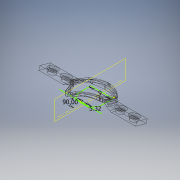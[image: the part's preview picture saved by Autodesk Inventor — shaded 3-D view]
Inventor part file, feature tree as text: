
AUTODESK INVENTOR PART (.ipt)
format: ipt  version: 2018 (Build 220112000, 112)  size: 2,753,024 bytes
history: native  units: mm
features: sketch x76, extrude x70, fillet x42, mirror x4, shell x1, hole x1, plane x1
ambient origin geometry x8: Origin, YZ Plane, XZ Plane, XY Plane, X Axis, Y Axis, Z Axis, Center Point
bodies: Solid1 (feature_tree)
feature tree (195):
  extrude  "Extrusion1"  TaperAngle=0.0deg  [1 undecoded]
  extrude  "Extrusion2"  Depth=10.0mm
  extrude  "Extrusion3"  TaperAngle=0.0deg  [1 undecoded]
  shell  "Shell2"  Thickness=0.0mm
  extrude  "Extrusion4"  Depth=1.6mm
  extrude  "Extrusion6"  Depth=10.0mm TaperAngle=0.0deg
  extrude  "Extrusion7"  Depth=1.75mm
  extrude  "Extrusion8"  Depth=2.0mm
  extrude  "Extrusion9"  Depth=10.0mm TaperAngle=0.0deg
  extrude  "Extrusion11"  Depth=10.0mm TaperAngle=0.0deg
  fillet  "Fillet1"  Radius=10.0mm
  fillet  "Fillet2"  Radius=10.0mm
  fillet  "Fillet3"  [1 undecoded]
  fillet  "Fillet4"  Radius=0.541mm
  fillet  "Fillet5"  [1 undecoded]
  extrude  "Extrusion12"  Depth=7.5mm TaperAngle=0.0deg
  extrude  "Extrusion13"  TaperAngle=0.0deg  [1 undecoded]
  extrude  "Extrusion16"  Depth=51.0mm TaperAngle=0.0deg
  extrude  "Extrusion17"  TaperAngle=0.0deg  [1 undecoded]
  extrude  "Extrusion18"  Depth=10.0mm TaperAngle=0.0deg
  extrude  "Extrusion19"  Depth=10.0mm TaperAngle=0.0deg
  fillet  "Fillet6"  Radius=6.0mm
  extrude  "Extrusion20"  Depth=42.0mm TaperAngle=0.0deg
  fillet  "Fillet7"  Radius=42.0mm
  extrude  "Extrusion21"  Depth=2.6mm
  extrude  "Extrusion22"  Depth=2.6mm
  sketch  "Sketch23"  dims[d147=12.0125mm d148=12.0125mm]
  extrude  "Extrusion24"  Depth=12.0125mm
  extrude  "Extrusion26"  Depth=17.5mm
  extrude  "Extrusion28"  Depth=3.0mm
  extrude  "Extrusion32"  Depth=3.0mm
  extrude  "Extrusion37"  Depth=12.0mm TaperAngle=0.0deg
  extrude  "Extrusion38"  Depth=10.0mm TaperAngle=0.0deg
  extrude  "Extrusion40"  Depth=3.11mm
  extrude  "Extrusion41"  Depth=10.0mm TaperAngle=0.0deg
  extrude  "Extrusion42"  Depth=0.365mm TaperAngle=0.0deg
  extrude  "Extrusion43"  TaperAngle=0.0deg  [1 undecoded]
  extrude  "Extrusion44"  TaperAngle=0.0deg  [1 undecoded]
  hole  "Hole1"  [1 undecoded]
  sketch  "Sketch45"  dims[d203=20.0mm d204=15.65mm d205=0.0mm]
  extrude  "Extrusion45"  Depth=15.65mm TaperAngle=0.0deg
  extrude  "Extrusion47"  Depth=0.861mm
  mirror  "Mirror1"
  extrude  "Extrusion48"  Depth=1.61mm
  fillet  "Fillet23"  [1 undecoded]
  fillet  "Fillet24"  Radius=1.92mm
  extrude  "Extrusion49"  Depth=0.276mm
  extrude  "Extrusion50"  TaperAngle=0.0deg  [1 undecoded]
  extrude  "Extrusion54"  TaperAngle=0.0deg  [1 undecoded]
  extrude  "Extrusion55"  Depth=2.5mm
  extrude  "Extrusion56"  TaperAngle=0.0deg  [1 undecoded]
  extrude  "Extrusion57"  Depth=10.0mm TaperAngle=0.0deg
  sketch  "Sketch61"  dims[d255=2.57mm d256=2.37mm]
  extrude  "Extrusion58"  Depth=0.83mm TaperAngle=0.0deg
  extrude  "Extrusion59"  Depth=2.37mm
  extrude  "Extrusion60"  Depth=4.5mm
  fillet  "Fillet27"  Radius=0.83mm
  fillet  "Fillet28"  Radius=6.37mm
  extrude  "Extrusion61"  Depth=6.37mm TaperAngle=0.0deg
  fillet  "Fillet29"  Radius=6.71mm
  fillet  "Fillet30"  Radius=6.71mm
  fillet  "Fillet31"  [1 undecoded]
  fillet  "Fillet32"  Radius=2.0mm
  extrude  "Extrusion62"  Depth=2.0mm
  fillet  "Fillet33"  Radius=2.0mm
  fillet  "Fillet34"  Radius=2.0mm
  fillet  "Fillet35"  Radius=2.0mm
  fillet  "Fillet36"  Radius=2.0mm
  extrude  "Extrusion63"  Depth=0.3mm
  extrude  "Extrusion64"  Depth=2.0mm
  extrude  "Extrusion65"  Depth=1.76mm TaperAngle=0.0deg
  fillet  "Fillet37"  [1 undecoded]
  fillet  "Fillet38"  Radius=0.6mm
  extrude  "Extrusion69"  Depth=0.323mm
  extrude  "Extrusion70"  Depth=6.7mm TaperAngle=0.0deg
  extrude  "Extrusion71"  Depth=2.0mm
  extrude  "Extrusion72"  TaperAngle=0.0deg  [1 undecoded]
  extrude  "Extrusion73"  Depth=2.0mm
  extrude  "Extrusion74"  Depth=5.47mm
  fillet  "Fillet42"  Radius=0.184mm
  fillet  "Fillet43"  [1 undecoded]
  extrude  "Extrusion75"  TaperAngle=90.0deg  [1 undecoded]
  extrude  "Extrusion76"  Depth=9.0mm
  mirror  "Mirror2"
  extrude  "Extrusion77"  [1 undecoded]
  extrude  "Extrusion78"  [1 undecoded]
  extrude  "Extrusion79"  [1 undecoded]
  mirror  "Mirror3"
  extrude  "Extrusion80"  [1 undecoded]
  extrude  "Extrusion81"  [1 undecoded]
  fillet  "Fillet44"  [1 undecoded]
  fillet  "Fillet45"  [1 undecoded]
  fillet  "Fillet46"  [1 undecoded]
  fillet  "Fillet47"  [1 undecoded]
  fillet  "Fillet48"  [1 undecoded]
  fillet  "Fillet49"  [1 undecoded]
  fillet  "Fillet50"  [1 undecoded]
  fillet  "Fillet51"  [1 undecoded]
  fillet  "Fillet52"  [1 undecoded]
  fillet  "Fillet53"  [1 undecoded]
  fillet  "Fillet54"  [1 undecoded]
  sketch  "Sketch87"
  extrude  "Extrusion82"  [1 undecoded]
  extrude  "Extrusion83"  [1 undecoded]
  extrude  "Extrusion84"  [1 undecoded]
  fillet  "Fillet55"  [1 undecoded]
  fillet  "Fillet56"  [1 undecoded]
  extrude  "Extrusion85"  [1 undecoded]
  extrude  "Extrusion86"  [1 undecoded]
  extrude  "Extrusion87"  [1 undecoded]
  fillet  "Fillet57"  [1 undecoded]
  fillet  "Fillet58"  [1 undecoded]
  extrude  "Extrusion88"  [1 undecoded]
  extrude  "Extrusion89"  [1 undecoded]
  fillet  "Fillet59"  [1 undecoded]
  fillet  "Fillet60"  [1 undecoded]
  fillet  "Fillet61"  [1 undecoded]
  fillet  "Fillet62"  [1 undecoded]
  extrude  "Extrusion90"  [1 undecoded]
  extrude  "Extrusion91"  [1 undecoded]
  sketch  "Sketch98"
  plane  "Work Plane1"
  mirror  "Mirror4"
  sketch  "Sketch99"
  extrude  "Extrusion92"  [1 undecoded]
  sketch  "Sketch1"  dims[d0=10.0mm d1=0.0mm d4=0.0mm d5=0.0mm]
  sketch  "Sketch2"  dims[d6=10.0mm d7=0.0mm d9=1.2mm]
  sketch  "Sketch3"  dims[d10=0.0mm d11=0.0mm d14=0.0mm d15=0.0mm d16=0.0mm d17=0.0mm]
  sketch  "Sketch4"  dims[d18=0.0mm d19=0.0mm d20=1.6mm]
  sketch  "Sketch6"  dims[d21=0.0mm d22=0.0mm d25=10.0mm d26=0.0mm]
  sketch  "Sketch7"  dims[d27=2.23mm d28=1.75mm]
  sketch  "Sketch8"  dims[d29=2.79mm d30=2.0mm]
  sketch  "Sketch9"  dims[d31=5.19mm d32=10.0mm d33=0.0mm]
  sketch  "Sketch11"  dims[d34=10.0mm d35=0.0mm d40=10.0mm d41=0.0mm d42=10.0mm d43=0.0mm d44=10.0mm d45=0.0mm d46=0.0mm d47=0.0mm d48=0.541mm d49=0.0mm d50=0.0mm]
  sketch  "Sketch12"  dims[d51=4.84mm d52=7.5mm d53=0.0mm]
  sketch  "Sketch13"  dims[d54=0.0mm d55=0.0mm d59=0.0mm d60=0.0mm]
  sketch  "Sketch16"  dims[d78=51.0mm d79=0.0mm d84=51.0mm d85=0.0mm]
  sketch  "Sketch17"  dims[d94=51.0mm d95=0.0mm d123=0.0mm d124=0.0mm]
  sketch  "Sketch18"  dims[d125=0.0mm d126=0.0mm d131=10.0mm d132=0.0mm]
  sketch  "Sketch19"  dims[d133=10.0mm d134=0.0mm d135=10.0mm d136=0.0mm d137=6.0mm]
  sketch  "Sketch20"  dims[d138=1.9mm d139=42.0mm d140=0.0mm d141=42.0mm d142=0.0mm]
  sketch  "Sketch21"  dims[d143=2.6mm d144=2.6mm]
  sketch  "Sketch22"  dims[d145=2.6mm d146=2.6mm]
  sketch  "Sketch24"  dims[d149=17.5mm d150=17.5mm]
  sketch  "Sketch26"  dims[d151=3.0mm d152=3.0mm]
  sketch  "Sketch28"  dims[d153=3.0mm d154=3.0mm]
  sketch  "Sketch32"  dims[d155=2.6mm d156=6.0mm d157=4.4mm d158=2.0mm d159=14.3117mm d160=8.0mm d161=20.594885mm d162=12.0mm d163=0.0mm]
  sketch  "Sketch37"  dims[d170=10.0mm d171=0.0mm d172=10.0mm d173=0.0mm]
  sketch  "Sketch38"  dims[d174=3.64mm d175=3.11mm]
  sketch  "Sketch40"  dims[d176=0.0mm d177=0.0mm d178=10.0mm d179=0.0mm]
  sketch  "Sketch41"  dims[d186=0.365mm d187=0.0mm d190=0.365mm d191=0.0mm]
  sketch  "Sketch42"  dims[d192=0.0mm d193=0.0mm d194=0.0mm d195=0.0mm]
  sketch  "Sketch43"  dims[d196=0.0mm d197=0.0mm d198=0.0mm d199=0.0mm]
  sketch  "Sketch44"  dims[d200=0.0mm d201=0.0mm d202=2.0mm]
  sketch  "Sketch46"  dims[d206=0.675mm d207=0.861mm]
  sketch  "Sketch48"  dims[d208=0.8mm d209=1.61mm d210=0.0mm d211=0.0mm d212=1.92mm]
  sketch  "Sketch49"  dims[d213=2.91mm d214=0.276mm]
  sketch  "Sketch50"  dims[d215=0.425mm d218=0.0mm d219=0.0mm]
  sketch  "Sketch51"  dims[d222=10.0mm d223=0.0mm d226=0.0mm d227=0.0mm]
  sketch  "Sketch55"  dims[d228=5.04mm d229=2.5mm]
  sketch  "Sketch57"  dims[d241=10.0mm d242=0.0mm d245=0.0mm d246=0.0mm]
  sketch  "Sketch59"  dims[d247=10.0mm d248=0.0mm d249=1.22mm d250=0.0mm]
  sketch  "Sketch60"  dims[d251=0.0mm d252=0.0mm d253=0.83mm d254=0.0mm]
  sketch  "Sketch62"  dims[d257=9.0mm d258=5.320111mm d259=8.0mm d260=4.5mm d261=0.83mm d262=0.0mm d263=6.37mm d264=0.0mm]
  sketch  "Sketch63"  dims[d265=6.37mm d266=0.0mm d267=6.37mm d268=0.0mm d269=6.71mm d270=0.0mm d271=6.71mm d272=0.0mm d273=0.0mm d274=0.0mm d275=2.0mm]
  sketch  "Sketch64"  dims[d276=0.789mm d277=2.0mm d278=2.0mm d279=2.0mm d280=2.0mm d281=2.0mm]
  sketch  "Sketch65"  dims[d285=1.9mm d286=0.3mm]
  sketch  "Sketch66"  dims[d287=0.616mm d288=2.0mm]
  sketch  "Sketch67"  dims[d289=2.0mm d290=1.76mm d291=0.0mm d292=0.0mm d293=0.0mm d294=0.6mm d295=0.0mm]
  sketch  "Sketch68"  dims[d296=0.409mm d297=0.323mm]
  sketch  "Sketch69"  dims[d298=6.7mm d299=0.0mm d300=6.7mm d301=0.0mm]
  sketch  "Sketch73"  dims[d302=0.0mm d303=0.0mm d304=2.0mm]
  sketch  "Sketch74"  dims[d305=2.0mm d306=0.0mm d307=0.0mm]
  sketch  "Sketch75"  dims[d308=6.7mm d309=0.0mm d310=2.0mm]
  sketch  "Sketch76"  dims[d311=0.241mm d312=5.47mm d313=0.184mm d314=0.0mm d315=0.0mm]
  sketch  "Sketch77"  dims[d316=10.0mm d317=0.0mm d318=90.0deg]
  sketch  "Sketch78"  dims[d319=0.9mm d321=9.0mm d322=5.320111mm]
  sketch  "Sketch79"  dims[d324=10.0mm d325=0.0mm]
  sketch  "Sketch80"
  sketch  "Sketch81"
  sketch  "Sketch82"
  sketch  "Sketch83"
  sketch  "Sketch84"
  sketch  "Sketch85"
  sketch  "Sketch88"
  sketch  "Sketch89"
  sketch  "Sketch90"
  sketch  "Sketch91"
  sketch  "Sketch92"
  sketch  "Sketch93"
  sketch  "Sketch94"
  sketch  "Sketch95"
  sketch  "Sketch96"
  sketch  "Sketch97"
  sketch  "Sketch100"
note: 53 required parameter values undecoded (feature->parameter linkage not recoverable at this tier; creation-order binding heuristic only, values carry confidence <= 0.55)
